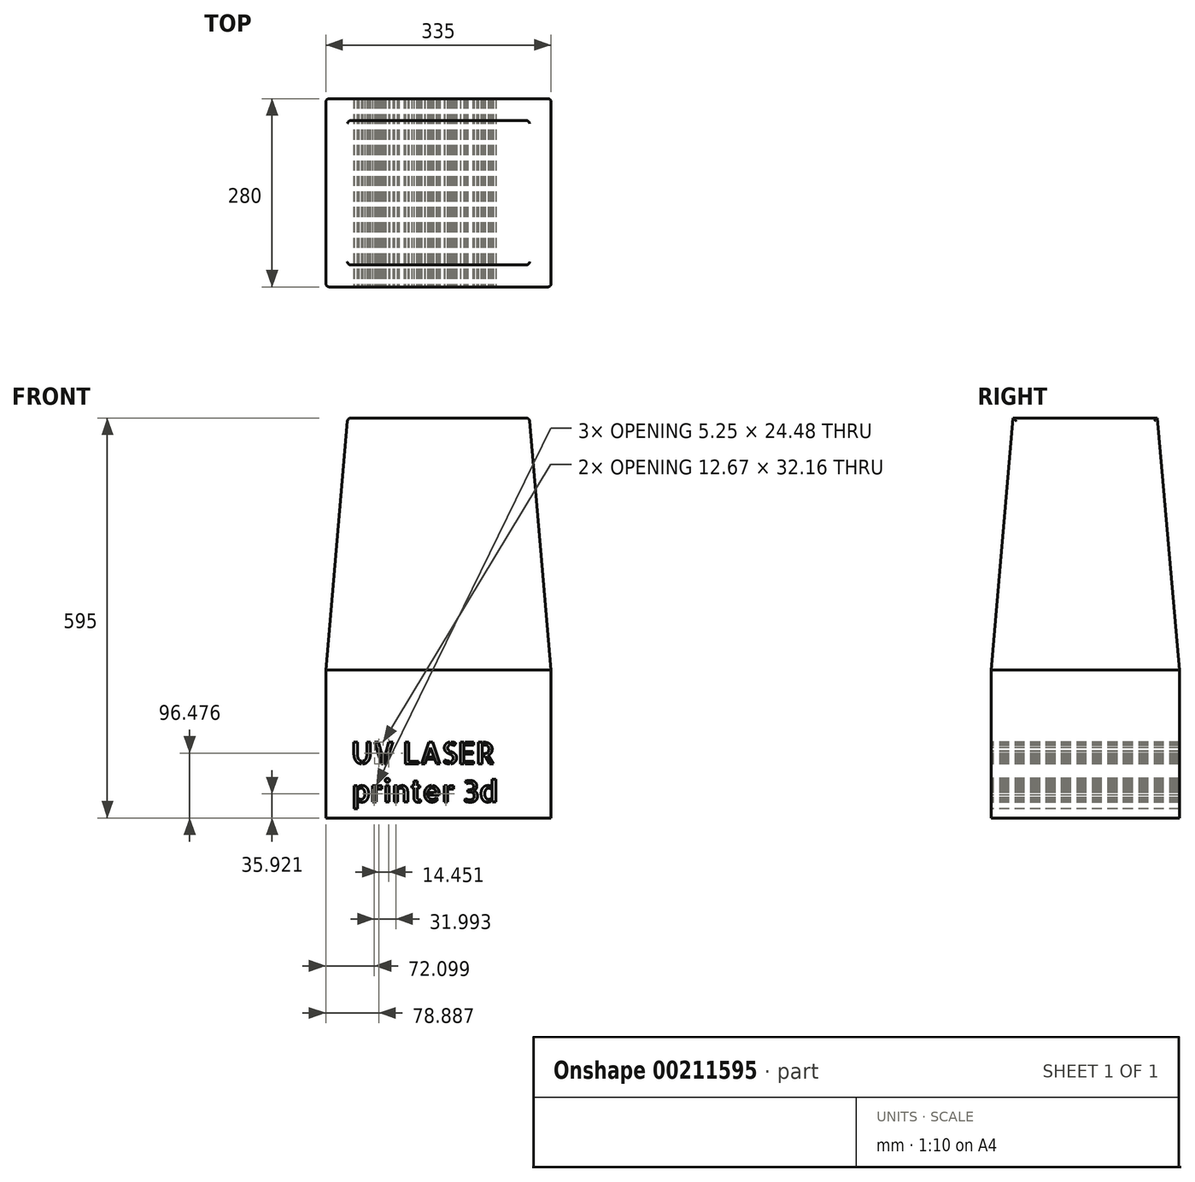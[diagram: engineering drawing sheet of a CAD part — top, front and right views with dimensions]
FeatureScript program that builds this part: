
annotation { "Feature Type Name" : "Feature", "Feature Type Description" : "" }
export const myFeature = defineFeature(function(context is Context, id is Id, definition is map)
    precondition{}
    {
        {
            var Q0;
            Q0=qCreatedBy(makeId("Front.planeOp"),FACE);
            var sketch = newSketch(context, id + "F0", { "sketchPlane" : qUnion([Q0])});
            skLineSegment(sketch, "E0.bottom", {"start": v(5, 0) * mm, "end": v(340, 0) * mm});
            skLineSegment(sketch, "E0.top", {"start": v(5, 220) * mm, "end": v(340, 220) * mm});
            skLineSegment(sketch, "E0.left", {"start": v(5, 0) * mm, "end": v(5, 220) * mm});
            skLineSegment(sketch, "E0.right", {"start": v(340, 0) * mm, "end": v(340, 220) * mm});
            skLineSegment(sketch, "E1", {"start": v(5, 220) * mm, "end": v(37.5, 595) * mm});
            skLineSegment(sketch, "E2", {"start": v(37.5, 595) * mm, "end": v(307.5, 595) * mm});
            skPoint(sketch, "E3", {"position": v(172.5, 595) * mm});
            skPoint(sketch, "E4", {"position": v(172.5, 220) * mm});
            skLineSegment(sketch, "E5", {"start": v(172.5, 96.75) * mm, "end": v(172.5, 59) * mm, "construction": true});
            skLineSegment(sketch, "E6.MirrorCS", {"start": v(340, 220) * mm, "end": v(307.5, 595) * mm});
            skSolve(sketch);
        }
        {
            var Q0;
            Q0=makeQuery(id+"F0.imprint","IMPRINT",FACE,{"disambiguationData":[TD([[makeQuery(id+"F0.imprint","IMPRINT",EDGE,{"derivedFrom":sQuery(id+"F0.wireOp",EDGE,"E0.bottom")}),1.0]])]});
            extrude(context, id + "F1", {"entities" : qUnion([Q0]), "oppositeDirection" : true, "depth" : 280 * mm});
        }
        {
            var Q0;
            Q0=makeQuery(id+"F0.imprint","IMPRINT",FACE,{"disambiguationData":[TD([[makeQuery(id+"F0.imprint","IMPRINT",EDGE,{"derivedFrom":sQuery(id+"F0.wireOp",EDGE,"E0.top")}),1.0]])]});
            var Q1;
            Q1=makeQuery(id+"F1.opExtrude","CAP_VERTEX",VERTEX,{"disambiguationData":[OSD([sQuery(id+"F0.wireOp",EDGE,"E0.top"),sQuery(id+"F0.wireOp",EDGE,"E0.left"),sQuery(id+"F0.wireOp",EDGE,"E1")])],"isStart":false});
            extrude(context, id + "F2", {"entities" : qUnion([Q0]), "endBound" : BoundingType.UP_TO_VERTEX, "oppositeDirection" : true, "endBoundEntityVertex" : qUnion([Q1]), "depth" : 25 * mm});
        }
        {
            var Q0;
            Q0=makeQuery(id+"F1.opExtrude","SWEPT_FACE",FACE,{"disambiguationData":[OSD([sQuery(id+"F0.wireOp",EDGE,"E0.left")])]});
            var sketch = newSketch(context, id + "F3", { "sketchPlane" : qUnion([Q0])});
            skLineSegment(sketch, "E7", {"start": v(-280, 220) * mm, "end": v(-247.5, 595) * mm});
            skLineSegment(sketch, "E8", {"start": v(-280, 220) * mm, "end": v(0, 220) * mm});
            skLineSegment(sketch, "E9", {"start": v(-140, 442.7) * mm, "end": v(-140, 486.9) * mm, "construction": true});
            skPoint(sketch, "E9.startSnap0", {"position": v(-140, 220) * mm});
            skLineSegment(sketch, "E10.MirrorCS", {"start": v(0, 220) * mm, "end": v(-32.5, 595) * mm});
            skLineSegment(sketch, "E11", {"start": v(-280, 220) * mm, "end": v(-280, 595) * mm});
            skLineSegment(sketch, "E12", {"start": v(-280, 595) * mm, "end": v(-247.5, 595) * mm});
            skLineSegment(sketch, "E13.MirrorCS", {"start": v(0, 595) * mm, "end": v(-32.5, 595) * mm});
            skLineSegment(sketch, "E14.MirrorCS", {"start": v(0, 220) * mm, "end": v(0, 595) * mm});
            skSolve(sketch);
        }
        {
            var Q0;
            Q0=makeQuery(id+"F3.imprint","IMPRINT",FACE,{"disambiguationData":[TD([[makeQuery(id+"F3.imprint","IMPRINT",EDGE,{"derivedFrom":sQuery(id+"F3.wireOp",EDGE,"E7")}),1.0]])]});
            var Q1;
            Q1=makeQuery(id+"F3.imprint","IMPRINT",FACE,{"disambiguationData":[TD([[makeQuery(id+"F3.imprint","IMPRINT",EDGE,{"derivedFrom":sQuery(id+"F3.wireOp",EDGE,"E10.MirrorCS")}),-1.0]])]});
            extrude(context, id + "F4", {"entities" : qUnion([Q0, Q1]), "operationType" : NewBodyOperationType.REMOVE, "oppositeDirection" : true, "depth" : 537 * mm});
        }
        {
            var Q0;
            Q0=makeQuery(id+"F0.imprint","IMPRINT",FACE,{"disambiguationData":[TD([[makeQuery(id+"F0.imprint","IMPRINT",EDGE,{"derivedFrom":sQuery(id+"F0.wireOp",EDGE,"E0.bottom")}),1.0]])]});
            var sketch = newSketch(context, id + "F5", { "sketchPlane" : qUnion([Q0])});
            skText(sketch, "E15", { "text": "UV LASER \nprinter 3d", "fontName": "AllertaStencil-Regular.ttf"});
            const initialGuessF5  = {"E15": [0.04296, 0.08057, 1, 0, 0.032]};
            skSetInitialGuess(sketch, initialGuessF5);
            skSolve(sketch);
        }
        {
            var Q0;
            Q0=makeQuery(id+"F5.imprint","IMPRINT",FACE,{"disambiguationData":[TD([[makeQuery(id+"F5.imprint","IMPRINT",EDGE,{"derivedFrom":sQuery(id+"F5.wireOp",EDGE,"E15.sketch_text.stroke-51")}),-1.0]])]});
            var Q1;
            Q1 = qSketchRegion(id + "F5", true);
            var Q2;
            Q2=makeQuery(id+"F5.imprint","IMPRINT",FACE,{"disambiguationData":[TD([[makeQuery(id+"F5.imprint","IMPRINT",EDGE,{"derivedFrom":sQuery(id+"F5.wireOp",EDGE,"E15.sketch_text.stroke-40")}),-1.0]])]});
            var Q3;
            Q3=makeQuery(id+"F5.imprint","IMPRINT",FACE,{"disambiguationData":[TD([[makeQuery(id+"F5.imprint","IMPRINT",EDGE,{"derivedFrom":sQuery(id+"F5.wireOp",EDGE,"E15.sketch_text.stroke-34")}),-1.0]])]});
            var Q4;
            Q4=makeQuery(id+"F5.imprint","IMPRINT",FACE,{"disambiguationData":[TD([[makeQuery(id+"F5.imprint","IMPRINT",EDGE,{"derivedFrom":sQuery(id+"F5.wireOp",EDGE,"E15.sketch_text.stroke-29")}),-1.0]])]});
            var Q5;
            Q5=makeQuery(id+"F5.imprint","IMPRINT",FACE,{"disambiguationData":[TD([[makeQuery(id+"F5.imprint","IMPRINT",EDGE,{"derivedFrom":sQuery(id+"F5.wireOp",EDGE,"E15.sketch_text.stroke-24")}),-1.0]])]});
            var Q6;
            Q6=makeQuery(id+"F5.imprint","IMPRINT",FACE,{"disambiguationData":[TD([[makeQuery(id+"F5.imprint","IMPRINT",EDGE,{"derivedFrom":sQuery(id+"F5.wireOp",EDGE,"E15.sketch_text.stroke-12")}),-1.0]])]});
            var Q7;
            Q7=makeQuery(id+"F5.imprint","IMPRINT",FACE,{"disambiguationData":[TD([[makeQuery(id+"F5.imprint","IMPRINT",EDGE,{"derivedFrom":sQuery(id+"F5.wireOp",EDGE,"E15.sketch_text.stroke-0")}),-1.0]])]});
            var Q8;
            Q8=makeQuery(id+"F5.imprint","IMPRINT",FACE,{"disambiguationData":[TD([[makeQuery(id+"F5.imprint","IMPRINT",EDGE,{"derivedFrom":sQuery(id+"F5.wireOp",EDGE,"E15.sketch_text.stroke-113")}),-1.0]])]});
            var Q9;
            Q9=makeQuery(id+"F5.imprint","IMPRINT",FACE,{"disambiguationData":[TD([[makeQuery(id+"F5.imprint","IMPRINT",EDGE,{"derivedFrom":sQuery(id+"F5.wireOp",EDGE,"E15.sketch_text.stroke-117")}),-1.0]])]});
            var Q10;
            Q10=makeQuery(id+"F5.imprint","IMPRINT",FACE,{"disambiguationData":[TD([[makeQuery(id+"F5.imprint","IMPRINT",EDGE,{"derivedFrom":sQuery(id+"F5.wireOp",EDGE,"E15.sketch_text.stroke-101")}),-1.0]])]});
            var Q11;
            Q11=makeQuery(id+"F5.imprint","IMPRINT",FACE,{"disambiguationData":[TD([[makeQuery(id+"F5.imprint","IMPRINT",EDGE,{"derivedFrom":sQuery(id+"F5.wireOp",EDGE,"E15.sketch_text.stroke-88")}),-1.0]])]});
            var Q12;
            Q12=makeQuery(id+"F5.imprint","IMPRINT",FACE,{"disambiguationData":[TD([[makeQuery(id+"F5.imprint","IMPRINT",EDGE,{"derivedFrom":sQuery(id+"F5.wireOp",EDGE,"E15.sketch_text.stroke-304")}),-1.0]])]});
            var Q13;
            Q13=makeQuery(id+"F5.imprint","IMPRINT",FACE,{"disambiguationData":[TD([[makeQuery(id+"F5.imprint","IMPRINT",EDGE,{"derivedFrom":sQuery(id+"F5.wireOp",EDGE,"E15.sketch_text.stroke-76")}),-1.0]])]});
            var Q14;
            Q14=makeQuery(id+"F5.imprint","IMPRINT",FACE,{"disambiguationData":[TD([[makeQuery(id+"F5.imprint","IMPRINT",EDGE,{"derivedFrom":sQuery(id+"F5.wireOp",EDGE,"E15.sketch_text.stroke-297")}),-1.0]])]});
            var Q15;
            Q15=makeQuery(id+"F5.imprint","IMPRINT",FACE,{"disambiguationData":[TD([[makeQuery(id+"F5.imprint","IMPRINT",EDGE,{"derivedFrom":sQuery(id+"F5.wireOp",EDGE,"E15.sketch_text.stroke-62")}),-1.0]])]});
            var Q16;
            Q16=makeQuery(id+"F5.imprint","IMPRINT",FACE,{"disambiguationData":[TD([[makeQuery(id+"F5.imprint","IMPRINT",EDGE,{"derivedFrom":sQuery(id+"F5.wireOp",EDGE,"E15.sketch_text.stroke-350")}),-1.0]])]});
            var Q17;
            Q17=makeQuery(id+"F5.imprint","IMPRINT",FACE,{"disambiguationData":[TD([[makeQuery(id+"F5.imprint","IMPRINT",EDGE,{"derivedFrom":sQuery(id+"F5.wireOp",EDGE,"E15.sketch_text.stroke-290")}),-1.0]])]});
            var Q18;
            Q18=makeQuery(id+"F5.imprint","IMPRINT",FACE,{"disambiguationData":[TD([[makeQuery(id+"F5.imprint","IMPRINT",EDGE,{"derivedFrom":sQuery(id+"F5.wireOp",EDGE,"E15.sketch_text.stroke-266")}),-1.0]])]});
            var Q19;
            Q19=makeQuery(id+"F5.imprint","IMPRINT",FACE,{"disambiguationData":[TD([[makeQuery(id+"F5.imprint","IMPRINT",EDGE,{"derivedFrom":sQuery(id+"F5.wireOp",EDGE,"E15.sketch_text.stroke-253")}),-1.0]])]});
            var Q20;
            Q20=makeQuery(id+"F5.imprint","IMPRINT",FACE,{"disambiguationData":[TD([[makeQuery(id+"F5.imprint","IMPRINT",EDGE,{"derivedFrom":sQuery(id+"F5.wireOp",EDGE,"E15.sketch_text.stroke-228")}),-1.0]])]});
            var Q21;
            Q21=makeQuery(id+"F5.imprint","IMPRINT",FACE,{"disambiguationData":[TD([[makeQuery(id+"F5.imprint","IMPRINT",EDGE,{"derivedFrom":sQuery(id+"F5.wireOp",EDGE,"E15.sketch_text.stroke-209")}),-1.0]])]});
            var Q22;
            Q22=makeQuery(id+"F5.imprint","IMPRINT",FACE,{"disambiguationData":[TD([[makeQuery(id+"F5.imprint","IMPRINT",EDGE,{"derivedFrom":sQuery(id+"F5.wireOp",EDGE,"E15.sketch_text.stroke-204")}),-1.0]])]});
            var Q23;
            Q23=makeQuery(id+"F5.imprint","IMPRINT",FACE,{"disambiguationData":[TD([[makeQuery(id+"F5.imprint","IMPRINT",EDGE,{"derivedFrom":sQuery(id+"F5.wireOp",EDGE,"E15.sketch_text.stroke-196")}),-1.0]])]});
            var Q24;
            Q24=makeQuery(id+"F5.imprint","IMPRINT",FACE,{"disambiguationData":[TD([[makeQuery(id+"F5.imprint","IMPRINT",EDGE,{"derivedFrom":sQuery(id+"F5.wireOp",EDGE,"E15.sketch_text.stroke-192")}),-1.0]])]});
            var Q25;
            Q25=makeQuery(id+"F5.imprint","IMPRINT",FACE,{"disambiguationData":[TD([[makeQuery(id+"F5.imprint","IMPRINT",EDGE,{"derivedFrom":sQuery(id+"F5.wireOp",EDGE,"E15.sketch_text.stroke-185")}),-1.0]])]});
            var Q26;
            Q26=makeQuery(id+"F5.imprint","IMPRINT",FACE,{"disambiguationData":[TD([[makeQuery(id+"F5.imprint","IMPRINT",EDGE,{"derivedFrom":sQuery(id+"F5.wireOp",EDGE,"E15.sketch_text.stroke-178")}),-1.0]])]});
            var Q27;
            Q27=makeQuery(id+"F5.imprint","IMPRINT",FACE,{"disambiguationData":[TD([[makeQuery(id+"F5.imprint","IMPRINT",EDGE,{"derivedFrom":sQuery(id+"F5.wireOp",EDGE,"E15.sketch_text.stroke-152")}),-1.0]])]});
            var Q28;
            Q28=makeQuery(id+"F5.imprint","IMPRINT",FACE,{"disambiguationData":[TD([[makeQuery(id+"F5.imprint","IMPRINT",EDGE,{"derivedFrom":sQuery(id+"F5.wireOp",EDGE,"E15.sketch_text.stroke-121")}),-1.0]])]});
            var Q29;
            Q29=makeQuery(id+"F5.imprint","IMPRINT",FACE,{"disambiguationData":[TD([[makeQuery(id+"F5.imprint","IMPRINT",EDGE,{"derivedFrom":sQuery(id+"F5.wireOp",EDGE,"E15.sketch_text.stroke-355")}),-1.0]])]});
            var Q30;
            Q30=makeQuery(id+"F5.imprint","IMPRINT",FACE,{"disambiguationData":[TD([[makeQuery(id+"F5.imprint","IMPRINT",EDGE,{"derivedFrom":sQuery(id+"F5.wireOp",EDGE,"E15.sketch_text.stroke-105")}),-1.0]])]});
            var Q31;
            Q31=makeQuery(id+"F5.imprint","IMPRINT",FACE,{"disambiguationData":[TD([[makeQuery(id+"F5.imprint","IMPRINT",EDGE,{"derivedFrom":sQuery(id+"F5.wireOp",EDGE,"E15.sketch_text.stroke-47")}),-1.0]])]});
            var Q32;
            Q32=makeQuery(id+"F5.imprint","IMPRINT",FACE,{"disambiguationData":[TD([[makeQuery(id+"F5.imprint","IMPRINT",EDGE,{"derivedFrom":sQuery(id+"F5.wireOp",EDGE,"E15.sketch_text.stroke-109")}),-1.0]])]});
            extrude(context, id + "F6", {"entities" : qUnion([Q0, Q1, Q2, Q3, Q4, Q5, Q6, Q7, Q8, Q9, Q10, Q11, Q12, Q13, Q14, Q15, Q16, Q17, Q18, Q19, Q20, Q21, Q22, Q23, Q24, Q25, Q26, Q27, Q28, Q29, Q30, Q31, Q32]), "operationType" : NewBodyOperationType.REMOVE, "oppositeDirection" : true, "depth" : 542 * mm});
        }
        {
            var Q0;
            Q0=makeQuery(id+"F4.boolean.opBoolean","COPY",EDGE,{"derivedFrom":makeQuery(id+"F4.opExtrude","SWEPT_EDGE",EDGE,{"disambiguationData":[OSD([sQuery(id+"F3.wireOp",EDGE,"E10.MirrorCS"),sQuery(id+"F3.wireOp",EDGE,"E13.MirrorCS")])]})});
            var Q1;
            Q1=makeQuery(id+"F1.opExtrude","CAP_EDGE",EDGE,{"disambiguationData":[OSD([sQuery(id+"F0.wireOp",EDGE,"E0.left")])],"isStart":true});
            var Q2;
            Q2=makeQuery(id+"F1.opExtrude","CAP_EDGE",EDGE,{"disambiguationData":[OSD([sQuery(id+"F0.wireOp",EDGE,"E0.right")])],"isStart":true});
            var Q3;
            Q3=makeQuery(id+"F1.opExtrude","CAP_EDGE",EDGE,{"disambiguationData":[OSD([sQuery(id+"F0.wireOp",EDGE,"E0.left")])],"isStart":false});
            var Q4;
            Q4=makeQuery(id+"F1.opExtrude","CAP_EDGE",EDGE,{"disambiguationData":[OSD([sQuery(id+"F0.wireOp",EDGE,"E0.right")])],"isStart":false});
            var Q5;
            Q5=makeQuery(id+"F4.boolean.opBoolean","INTERSECT",EDGE,{"derivedFrom":[makeQuery(id+"F2.opExtrude","SWEPT_FACE",FACE,{"disambiguationData":[OSD([sQuery(id+"F0.wireOp",EDGE,"E6.MirrorCS")])]}),makeQuery(id+"F4.opExtrude","SWEPT_FACE",FACE,{"disambiguationData":[OSD([sQuery(id+"F3.wireOp",EDGE,"E7")])]})]});
            var Q6;
            Q6=makeQuery(id+"F2.opExtrude","SWEPT_EDGE",EDGE,{"disambiguationData":[OSD([sQuery(id+"F0.wireOp",EDGE,"E2"),sQuery(id+"F0.wireOp",EDGE,"E6.MirrorCS")])]});
            var Q7;
            Q7=makeQuery(id+"F4.boolean.opBoolean","COPY",EDGE,{"derivedFrom":makeQuery(id+"F4.opExtrude","SWEPT_EDGE",EDGE,{"disambiguationData":[OSD([sQuery(id+"F3.wireOp",EDGE,"E7"),sQuery(id+"F3.wireOp",EDGE,"E12")])]})});
            var Q8;
            Q8=makeQuery(id+"F4.boolean.opBoolean","INTERSECT",EDGE,{"derivedFrom":[makeQuery(id+"F2.opExtrude","SWEPT_FACE",FACE,{"disambiguationData":[OSD([sQuery(id+"F0.wireOp",EDGE,"E1")])]}),makeQuery(id+"F4.opExtrude","SWEPT_FACE",FACE,{"disambiguationData":[OSD([sQuery(id+"F3.wireOp",EDGE,"E7")])]})]});
            var Q9;
            Q9=makeQuery(id+"F4.boolean.opBoolean","INTERSECT",EDGE,{"derivedFrom":[makeQuery(id+"F2.opExtrude","SWEPT_FACE",FACE,{"disambiguationData":[OSD([sQuery(id+"F0.wireOp",EDGE,"E1")])]}),makeQuery(id+"F4.opExtrude","SWEPT_FACE",FACE,{"disambiguationData":[OSD([sQuery(id+"F3.wireOp",EDGE,"E10.MirrorCS")])]})]});
            var Q10;
            Q10=makeQuery(id+"F2.opExtrude","SWEPT_EDGE",EDGE,{"disambiguationData":[OSD([sQuery(id+"F0.wireOp",EDGE,"E1"),sQuery(id+"F0.wireOp",EDGE,"E2")])]});
            var Q11;
            Q11=makeQuery(id+"F4.boolean.opBoolean","INTERSECT",EDGE,{"derivedFrom":[makeQuery(id+"F2.opExtrude","SWEPT_FACE",FACE,{"disambiguationData":[OSD([sQuery(id+"F0.wireOp",EDGE,"E6.MirrorCS")])]}),makeQuery(id+"F4.opExtrude","SWEPT_FACE",FACE,{"disambiguationData":[OSD([sQuery(id+"F3.wireOp",EDGE,"E10.MirrorCS")])]})]});
            fillet(context, id + "F7", {"entities" : qUnion([Q0, Q1, Q2, Q3, Q4, Q5, Q6, Q7, Q8, Q9, Q10, Q11]), "radius" : 5 * mm, "tangentPropagation" : true, "allowEdgeOverflow" : false});
        }
    });
